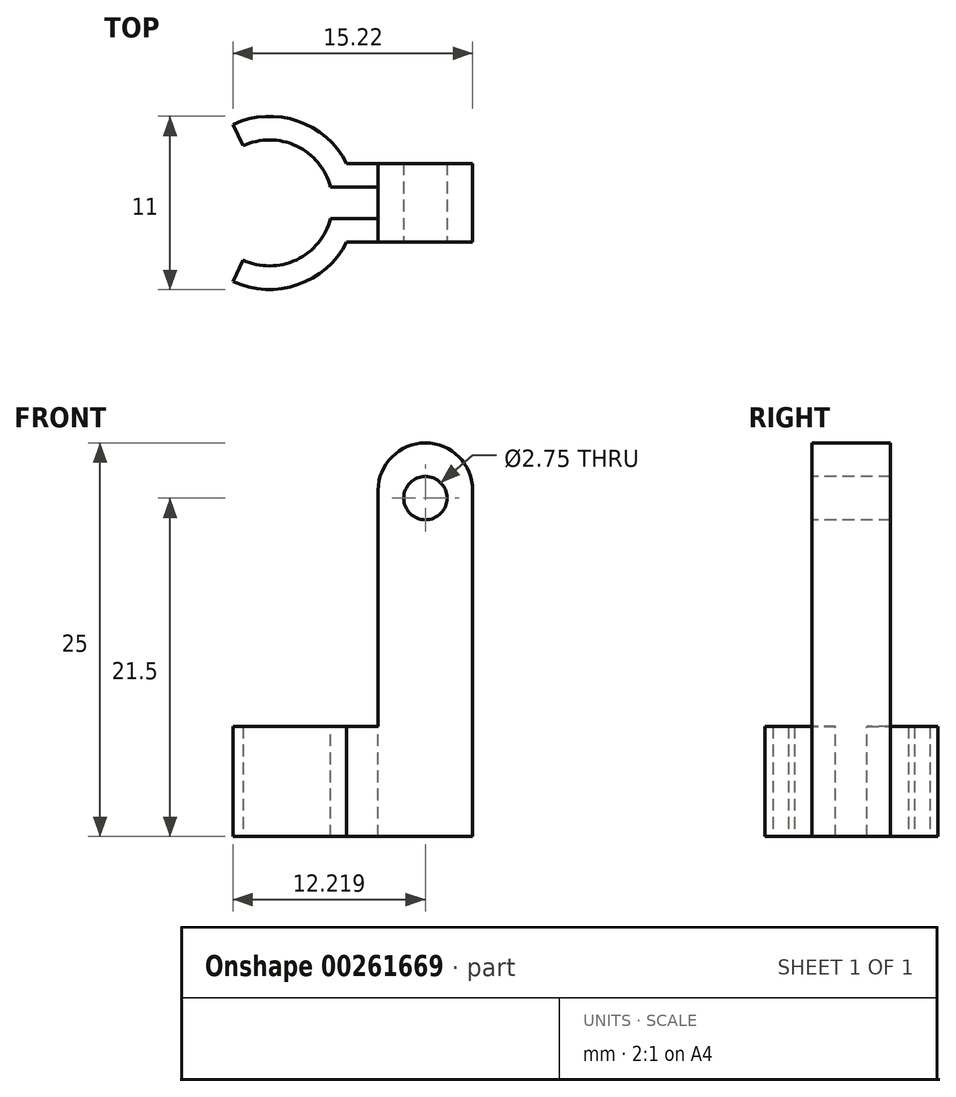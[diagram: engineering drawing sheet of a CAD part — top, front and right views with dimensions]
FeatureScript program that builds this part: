
annotation { "Feature Type Name" : "Feature", "Feature Type Description" : "" }
export const myFeature = defineFeature(function(context is Context, id is Id, definition is map)
    precondition{}
    {
        {
            var Q0;
            Q0=qCreatedBy(makeId("Top.planeOp"),FACE);
            var sketch = newSketch(context, id + "F0", { "sketchPlane" : qUnion([Q0])});
            skCircle(sketch, "E0", {"center": v(0, 0) * mm, "radius": 4 * mm});
            skCircle(sketch, "E1", {"center": v(0, 0) * mm, "radius": 5.5 * mm});
            skLineSegment(sketch, "E2", {"start": v(4.9, 2.5) * mm, "end": v(12.9, 2.5) * mm});
            skLineSegment(sketch, "E3.MirrorCS", {"start": v(4.9, -2.5) * mm, "end": v(12.9, -2.5) * mm});
            skLineSegment(sketch, "E4", {"start": v(12.9, 2.5) * mm, "end": v(12.9, -2.5) * mm});
            skLineSegment(sketch, "E5", {"start": v(6.9, 2.5) * mm, "end": v(6.9, -2.5) * mm});
            skLineSegment(sketch, "E6", {"start": v(0, 0) * mm, "end": v(-2.32, 4.98) * mm});
            skLineSegment(sketch, "E7.MirrorCS", {"start": v(0, 0) * mm, "end": v(-2.32, -4.98) * mm});
            skSolve(sketch);
        }
        {
            var Q0;
            {var subQ5=sQuery(id+"F0.wireOp",EDGE,"E0");var subQ7=sQuery(id+"F0.wireOp",EDGE,"E6");var subQ9=makeQuery(id+"F0.imprint","INTERSECT",VERTEX,{"derivedFrom":[subQ5,subQ7]});Q0=makeQuery(id+"F0.imprint","IMPRINT",FACE,{"disambiguationData":[TD([[makeQuery(id+"F0.imprint","IMPRINT",EDGE,{"disambiguationData":[TD([[subQ9,1.0]])],"derivedFrom":subQ5}),-1.0]])]});}
            var Q1;
            {var subQ5=sQuery(id+"F0.wireOp",EDGE,"E5");Q1=makeQuery(id+"F0.imprint","IMPRINT",FACE,{"disambiguationData":[TD([[makeQuery(id+"F0.imprint","IMPRINT",EDGE,{"derivedFrom":subQ5}),-1.0]])]});}
            extrude(context, id + "F1", {"entities" : qUnion([Q0, Q1]), "depth" : 7 * mm});
        }
        {
            var Q0;
            {var subQ0=sQuery(id+"F0.wireOp",EDGE,"E4");Q0=makeQuery(id+"F0.imprint","IMPRINT",FACE,{"disambiguationData":[TD([[makeQuery(id+"F0.imprint","IMPRINT",EDGE,{"derivedFrom":subQ0}),-1.0]])]});}
            extrude(context, id + "F2", {"entities" : qUnion([Q0]), "operationType" : NewBodyOperationType.ADD, "depth" : 25 * mm});
        }
        {
            var Q0;
            {var subQ0=sQuery(id+"F0.wireOp",EDGE,"E3.MirrorCS");Q0=makeQuery(id+"F2.boolean.opBoolean","MERGE",FACE,{"derivedFrom":[makeQuery(id+"F1.opExtrude","SWEPT_FACE",FACE,{"disambiguationData":[OSD([subQ0])]}),makeQuery(id+"F2.opExtrude","SWEPT_FACE",FACE,{"disambiguationData":[OSD([subQ0])]})]});}
            var sketch = newSketch(context, id + "F3", { "sketchPlane" : qUnion([Q0])});
            skCircle(sketch, "E8", {"center": v(9.9, 21.5) * mm, "radius": 1.37 * mm});
            skPoint(sketch, "E8.centerSnap0", {"position": v(9.9, 25) * mm});
            skSolve(sketch);
        }
        {
            var Q0;
            Q0=makeQuery(id+"F3.imprint","IMPRINT",FACE,{"disambiguationData":[TD([[makeQuery(id+"F3.imprint","IMPRINT",EDGE,{"derivedFrom":sQuery(id+"F3.wireOp",EDGE,"E8")}),1.0]])]});
            extrude(context, id + "F4", {"entities" : qUnion([Q0]), "operationType" : NewBodyOperationType.REMOVE, "oppositeDirection" : true, "depth" : 25 * mm});
        }
        {
            var Q0;
            Q0=makeQuery(id+"F2.opExtrude","CAP_EDGE",EDGE,{"disambiguationData":[OSD([sQuery(id+"F0.wireOp",EDGE,"E4")])],"isStart":false});
            var Q1;
            Q1=makeQuery(id+"F2.opExtrude","CAP_EDGE",EDGE,{"disambiguationData":[OSD([sQuery(id+"F0.wireOp",EDGE,"E5")])],"isStart":false});
            fillet(context, id + "F5", {"entities" : qUnion([Q0, Q1]), "radius" : 3 * mm, "tangentPropagation" : true, "allowEdgeOverflow" : false});
        }
        {
            var Q0;
            Q0=makeQuery(id+"F1.opExtrude","CAP_FACE",FACE,{"disambiguationData":[OSD([sQuery(id+"F0.wireOp",EDGE,"E0"),sQuery(id+"F0.wireOp",EDGE,"E1"),sQuery(id+"F0.wireOp",EDGE,"E2"),sQuery(id+"F0.wireOp",EDGE,"E3.MirrorCS"),sQuery(id+"F0.wireOp",EDGE,"E5"),sQuery(id+"F0.wireOp",EDGE,"E6"),sQuery(id+"F0.wireOp",EDGE,"E7.MirrorCS")])],"isStart":false});
            var sketch = newSketch(context, id + "F6", { "sketchPlane" : qUnion([Q0])});
            skLineSegment(sketch, "E9.bottom", {"start": v(6.9, -1) * mm, "end": v(2.9, -1) * mm});
            skLineSegment(sketch, "E9.top", {"start": v(6.9, 1) * mm, "end": v(2.9, 1) * mm});
            skLineSegment(sketch, "E9.left", {"start": v(6.9, -1) * mm, "end": v(6.9, 1) * mm});
            skLineSegment(sketch, "E9.right", {"start": v(2.9, -1) * mm, "end": v(2.9, 1) * mm});
            skPoint(sketch, "E9.middle", {"position": v(4.9, 0) * mm});
            skSolve(sketch);
        }
        {
            var Q0;
            {var subQ0=sQuery(id+"F6.wireOp",EDGE,"E9.left");Q0=makeQuery(id+"F6.imprint","IMPRINT",FACE,{"disambiguationData":[TD([[makeQuery(id+"F6.imprint","IMPRINT",EDGE,{"derivedFrom":subQ0}),-1.0]])]});}
            extrude(context, id + "F7", {"entities" : qUnion([Q0]), "operationType" : NewBodyOperationType.REMOVE, "oppositeDirection" : true, "depth" : 25 * mm});
        }
    });
